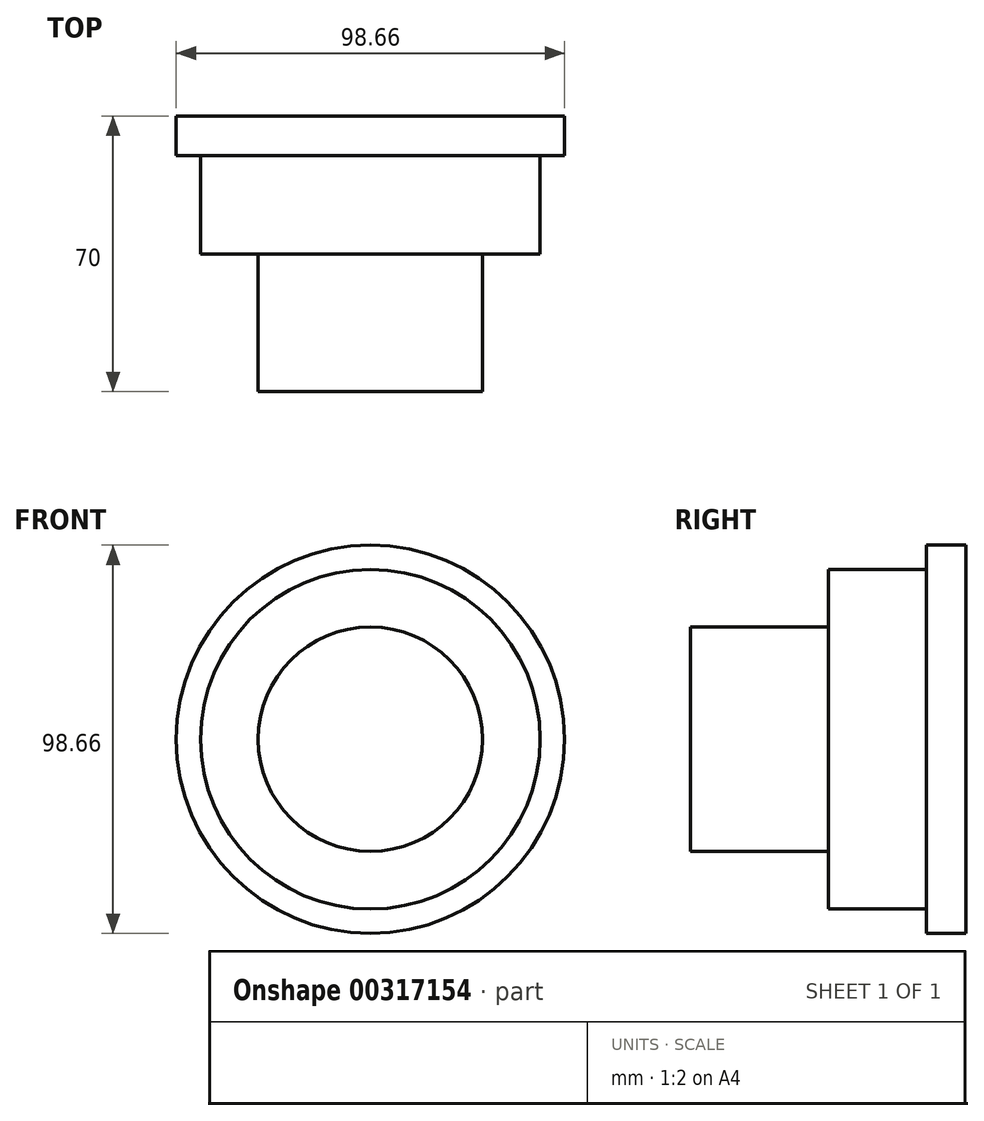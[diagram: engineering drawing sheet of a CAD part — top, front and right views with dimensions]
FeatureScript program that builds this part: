
annotation { "Feature Type Name" : "Feature", "Feature Type Description" : "" }
export const myFeature = defineFeature(function(context is Context, id is Id, definition is map)
    precondition{}
    {
        {
            var Q0;
            Q0=qCreatedBy(makeId("Front.planeOp"),FACE);
            var sketch = newSketch(context, id + "F0", { "sketchPlane" : qUnion([Q0])});
            skCircle(sketch, "E0", {"center": v(0, 0) * mm, "radius": 49.32 * mm});
            skSolve(sketch);
        }
        {
            var Q0;
            Q0 = qSketchRegion(id + "F0", true);
            extrude(context, id + "F1", {"entities" : qUnion([Q0]), "depth" : 35 * mm});
        }
        {
            var Q0;
            Q0=makeQuery(id+"F1.opExtrude","CAP_FACE",FACE,{"disambiguationData":[OSD([sQuery(id+"F0.wireOp",EDGE,"E0")])],"isStart":false});
            var sketch = newSketch(context, id + "F2", { "sketchPlane" : qUnion([Q0])});
            skCircle(sketch, "E1", {"center": v(0, 0) * mm, "radius": 50.95 * mm});
            skCircle(sketch, "E2", {"center": v(0, 0) * mm, "radius": 43.14 * mm});
            skSolve(sketch);
        }
        {
            var Q0;
            Q0 = qSketchRegion(id + "F2", true);
            extrude(context, id + "F3", {"entities" : qUnion([Q0]), "operationType" : NewBodyOperationType.REMOVE, "oppositeDirection" : true, "depth" : 25 * mm});
        }
        {
            var Q0;
            Q0=makeQuery(id+"F1.opExtrude","CAP_FACE",FACE,{"disambiguationData":[OSD([sQuery(id+"F0.wireOp",EDGE,"E0")])],"isStart":false});
            var sketch = newSketch(context, id + "F4", { "sketchPlane" : qUnion([Q0])});
            skCircle(sketch, "E3", {"center": v(0, 0) * mm, "radius": 28.5 * mm});
            skSolve(sketch);
        }
        {
            var Q0;
            Q0 = qSketchRegion(id + "F4", true);
            extrude(context, id + "F5", {"entities" : qUnion([Q0]), "operationType" : NewBodyOperationType.ADD, "depth" : 35 * mm});
        }
    });
